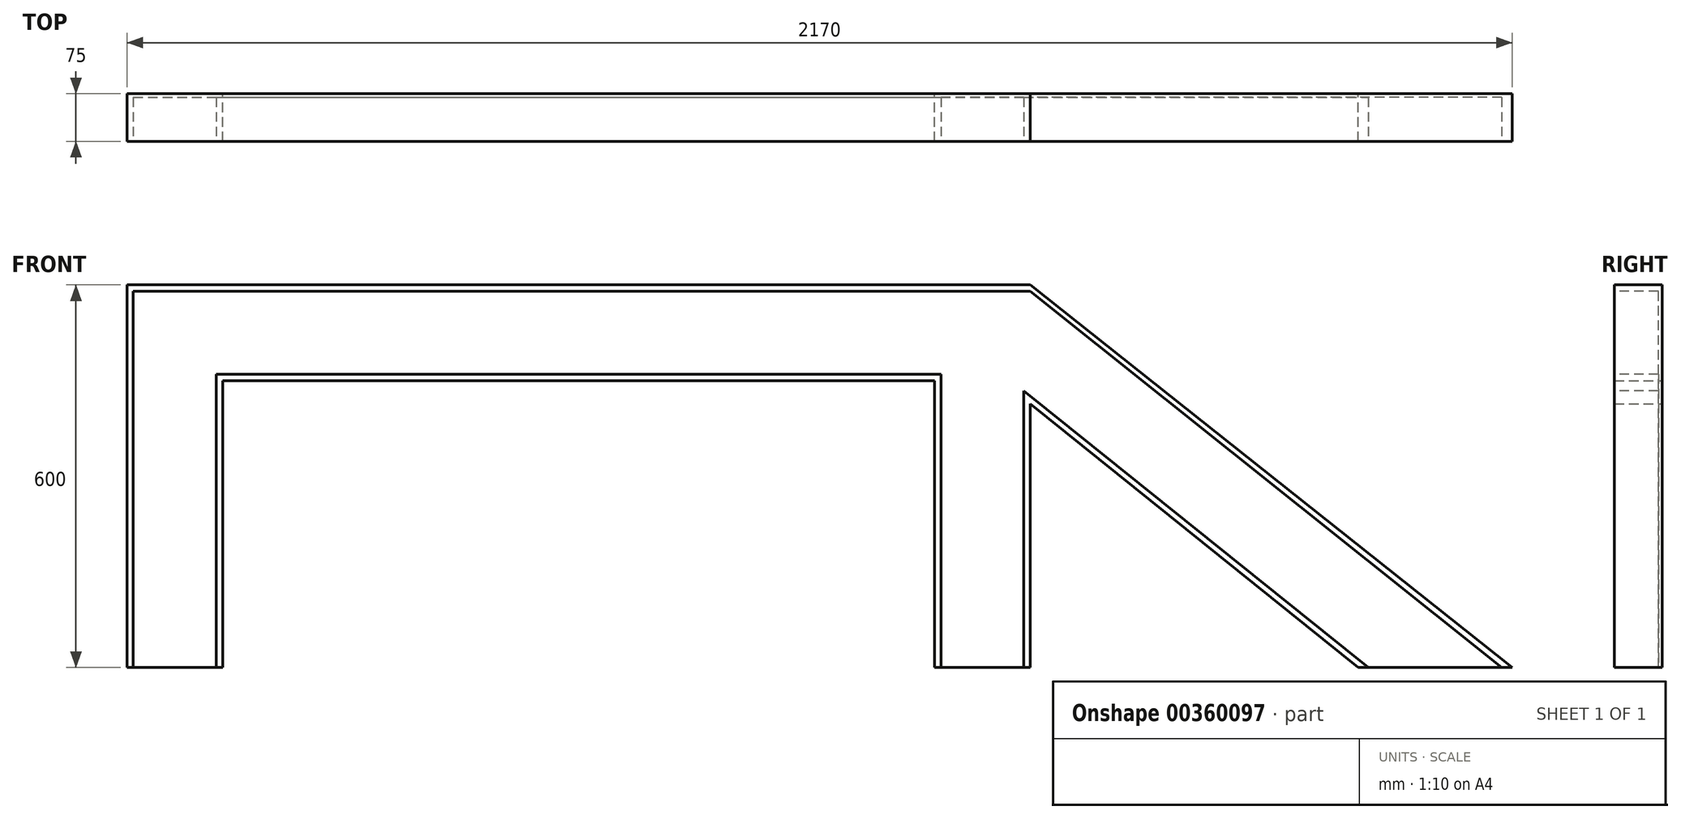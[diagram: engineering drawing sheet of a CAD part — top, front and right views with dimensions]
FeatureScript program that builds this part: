
annotation { "Feature Type Name" : "Feature", "Feature Type Description" : "" }
export const myFeature = defineFeature(function(context is Context, id is Id, definition is map)
    precondition{}
    {
        {
            var Q0;
            Q0=qCreatedBy(makeId("Front.planeOp"),FACE);
            var sketch = newSketch(context, id + "F0", { "sketchPlane" : qUnion([Q0])});
            skLineSegment(sketch, "E0", {"start": v(0, 0) * mm, "end": v(0, 600) * mm});
            skLineSegment(sketch, "E1", {"start": v(0, 600) * mm, "end": v(1415, 600) * mm});
            skLineSegment(sketch, "E2", {"start": v(2170, 0) * mm, "end": v(1415, 600) * mm});
            skLineSegment(sketch, "E3", {"start": v(0, 0) * mm, "end": v(150, 0) * mm});
            skLineSegment(sketch, "E4", {"start": v(1415, 0) * mm, "end": v(1265, 0) * mm});
            skLineSegment(sketch, "E5", {"start": v(1265, 0) * mm, "end": v(1265, 450) * mm});
            skLineSegment(sketch, "E6", {"start": v(150, 0) * mm, "end": v(150, 450) * mm});
            skLineSegment(sketch, "E7", {"start": v(150, 450) * mm, "end": v(1265, 450) * mm});
            skLineSegment(sketch, "E8", {"start": v(1415, 413.25) * mm, "end": v(1415, 0) * mm});
            skLineSegment(sketch, "E9", {"start": v(2170, 0) * mm, "end": v(1928.9, 0) * mm});
            skLineSegment(sketch, "E10", {"start": v(1928.9, 0) * mm, "end": v(1415, 413.25) * mm});
            skSolve(sketch);
        }
        {
            var Q0;
            Q0 = qSketchRegion(id + "F0", true);
            extrude(context, id + "F1", {"entities" : qUnion([Q0]), "depth" : 75 * mm});
        }
        {
            var Q0;
            Q0=makeQuery(id+"F1.opExtrude","CAP_FACE",FACE,{"disambiguationData":[OSD([sQuery(id+"F0.wireOp",EDGE,"E0"),sQuery(id+"F0.wireOp",EDGE,"E1"),sQuery(id+"F0.wireOp",EDGE,"E2"),sQuery(id+"F0.wireOp",EDGE,"E3"),sQuery(id+"F0.wireOp",EDGE,"E4"),sQuery(id+"F0.wireOp",EDGE,"E5"),sQuery(id+"F0.wireOp",EDGE,"E6"),sQuery(id+"F0.wireOp",EDGE,"E7"),sQuery(id+"F0.wireOp",EDGE,"E8"),sQuery(id+"F0.wireOp",EDGE,"E9"),sQuery(id+"F0.wireOp",EDGE,"E10")])],"isStart":false});
            var sketch = newSketch(context, id + "F2", { "sketchPlane" : qUnion([Q0])});
            skLineSegment(sketch, "E11", {"start": v(0, 600) * mm, "end": v(10, 600) * mm});
            skLineSegment(sketch, "E12", {"start": v(140, 450) * mm, "end": v(140, 0) * mm});
            skLineSegment(sketch, "E13", {"start": v(140, 450) * mm, "end": v(140, 460) * mm});
            skLineSegment(sketch, "E14", {"start": v(140, 460) * mm, "end": v(1265.2, 460) * mm});
            skLineSegment(sketch, "E15", {"start": v(10, 590) * mm, "end": v(10, 0) * mm});
            skLineSegment(sketch, "E16", {"start": v(1265.2, 460) * mm, "end": v(1275.2, 460) * mm});
            skLineSegment(sketch, "E17", {"start": v(1275.2, 460) * mm, "end": v(1275.2, 0) * mm});
            skLineSegment(sketch, "E18", {"start": v(1405, 0) * mm, "end": v(1405, 434.12) * mm});
            skLineSegment(sketch, "E19", {"start": v(1405, 434.12) * mm, "end": v(1944.86, 0) * mm});
            skLineSegment(sketch, "E20", {"start": v(2153.76, 0) * mm, "end": v(1415, 590) * mm});
            skLineSegment(sketch, "E21", {"start": v(10, 590) * mm, "end": v(1415, 590) * mm});
            skLineSegment(sketch, "E22", {"start": v(2153.76, 0) * mm, "end": v(1944.86, 0) * mm});
            skLineSegment(sketch, "E23", {"start": v(1405, 0) * mm, "end": v(1275.2, 0) * mm});
            skLineSegment(sketch, "E24", {"start": v(10, 0) * mm, "end": v(140, 0) * mm});
            skSolve(sketch);
        }
        {
            var Q0;
            Q0 = qSketchRegion(id + "F2", true);
            extrude(context, id + "F3", {"entities" : qUnion([Q0]), "operationType" : NewBodyOperationType.REMOVE, "oppositeDirection" : true, "depth" : 69 * mm});
        }
    });
